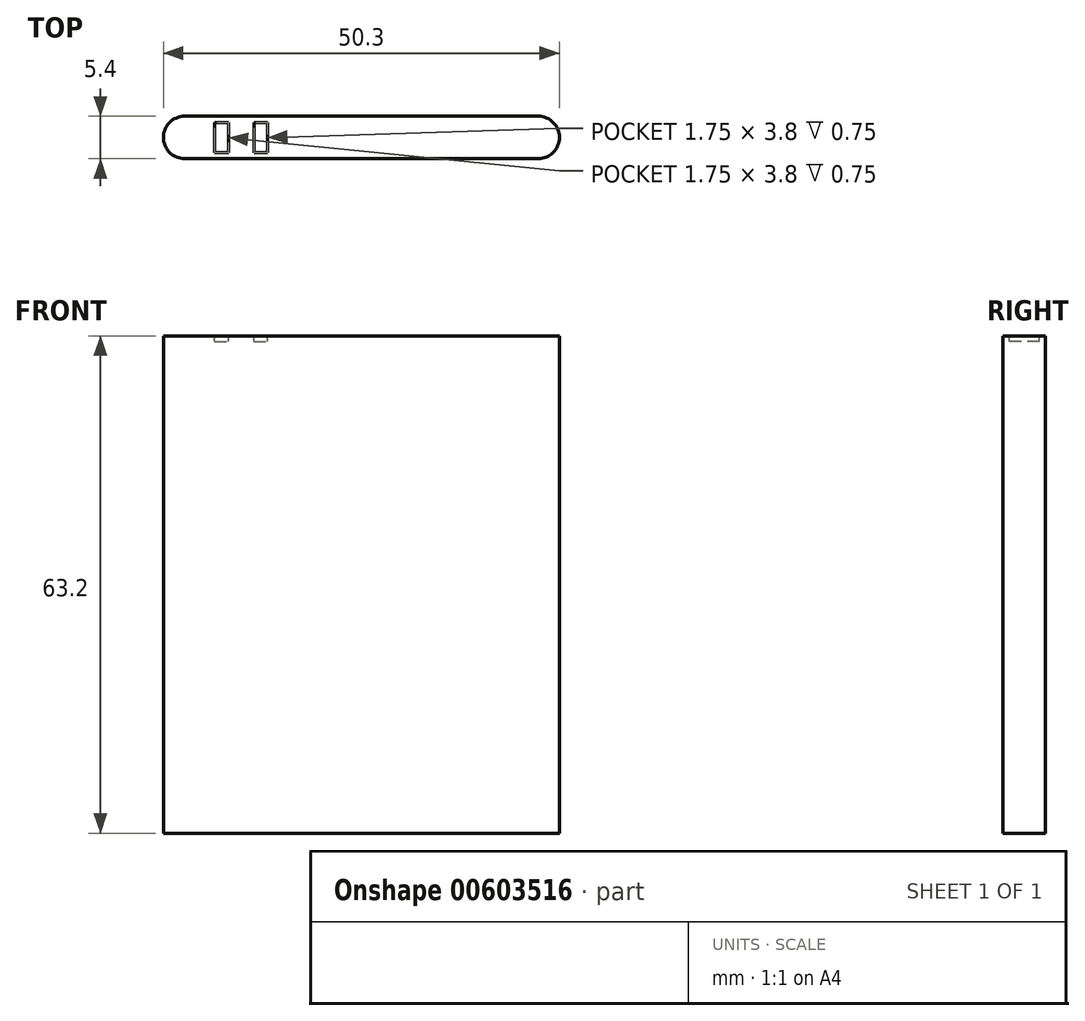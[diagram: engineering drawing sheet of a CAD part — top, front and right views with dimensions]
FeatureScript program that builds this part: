
annotation { "Feature Type Name" : "Feature", "Feature Type Description" : "" }
export const myFeature = defineFeature(function(context is Context, id is Id, definition is map)
    precondition{}
    {
        {
            var Q0;
            Q0=qCreatedBy(makeId("Front.planeOp"),FACE);
            var sketch = newSketch(context, id + "F0", { "sketchPlane" : qUnion([Q0])});
            skLineSegment(sketch, "E0.bottom", {"start": v(25.15, -31.6) * mm, "end": v(-25.15, -31.6) * mm});
            skLineSegment(sketch, "E0.top", {"start": v(25.15, 31.6) * mm, "end": v(-25.15, 31.6) * mm});
            skLineSegment(sketch, "E0.left", {"start": v(25.15, -31.6) * mm, "end": v(25.15, 31.6) * mm});
            skLineSegment(sketch, "E0.right", {"start": v(-25.15, -31.6) * mm, "end": v(-25.15, 31.6) * mm});
            skPoint(sketch, "E0.middle", {"position": v(0, 0) * mm});
            skSolve(sketch);
        }
        {
            var Q0;
            Q0=makeQuery(id+"F0.imprint","IMPRINT",FACE,{"disambiguationData":[TD([[makeQuery(id+"F0.imprint","IMPRINT",EDGE,{"derivedFrom":sQuery(id+"F0.wireOp",EDGE,"E0.bottom")}),-1.0]])]});
            extrude(context, id + "F1", {"entities" : qUnion([Q0]), "endBound" : BoundingType.SYMMETRIC, "depth" : 5.4 * mm, "offsetDistance" : 25 * mm});
        }
        {
            var Q0;
            Q0=makeQuery(id+"F1.opExtrude","CAP_EDGE",EDGE,{"disambiguationData":[OSD([sQuery(id+"F0.wireOp",EDGE,"E0.left")])],"isStart":true});
            var Q1;
            Q1=makeQuery(id+"F1.opExtrude","CAP_EDGE",EDGE,{"disambiguationData":[OSD([sQuery(id+"F0.wireOp",EDGE,"E0.left")])],"isStart":false});
            var Q2;
            Q2=makeQuery(id+"F1.opExtrude","CAP_EDGE",EDGE,{"disambiguationData":[OSD([sQuery(id+"F0.wireOp",EDGE,"E0.right")])],"isStart":false});
            var Q3;
            Q3=makeQuery(id+"F1.opExtrude","CAP_EDGE",EDGE,{"disambiguationData":[OSD([sQuery(id+"F0.wireOp",EDGE,"E0.right")])],"isStart":true});
            fillet(context, id + "F2", {"entities" : qUnion([Q0, Q1, Q2, Q3]), "radius" : 2.7 * mm, "tangentPropagation" : true, "allowEdgeOverflow" : false});
        }
        {
            var Q0;
            Q0=makeQuery(id+"F1.opExtrude","SWEPT_FACE",FACE,{"disambiguationData":[OSD([sQuery(id+"F0.wireOp",EDGE,"E0.top")])]});
            var sketch = newSketch(context, id + "F3", { "sketchPlane" : qUnion([Q0])});
            skLineSegment(sketch, "E1", {"start": v(-24.37, 1.9) * mm, "end": v(24.37, 1.9) * mm, "construction": true});
            skLineSegment(sketch, "E2", {"start": v(-24.37, -1.9) * mm, "end": v(24.37, -1.9) * mm, "construction": true});
            skLineSegment(sketch, "E3.0.0", {"start": v(22.45, 2.7) * mm, "end": v(-22.45, 2.7) * mm, "construction": true});
            skArc(sketch, "E3.0.1", {"start": v(-22.45, 2.7) * mm, "mid": v(-25.15, 0) * mm, "end": v(-22.45, -2.7) * mm, "construction": true});
            skLineSegment(sketch, "E3.0.2", {"start": v(-22.45, -2.7) * mm, "end": v(22.45, -2.7) * mm, "construction": true});
            skArc(sketch, "E3.0.3", {"start": v(22.45, -2.7) * mm, "mid": v(25.15, 0) * mm, "end": v(22.45, 2.7) * mm, "construction": true});
            skLineSegment(sketch, "E4.bottom", {"start": v(-18.65, 1.9) * mm, "end": v(-16.9, 1.9) * mm});
            skLineSegment(sketch, "E4.top", {"start": v(-18.65, -1.9) * mm, "end": v(-16.9, -1.9) * mm});
            skLineSegment(sketch, "E4.left", {"start": v(-18.65, 1.9) * mm, "end": v(-18.65, -1.9) * mm});
            skLineSegment(sketch, "E4.right", {"start": v(-16.9, 1.9) * mm, "end": v(-16.9, -1.9) * mm});
            skLineSegment(sketch, "E5.bottom", {"start": v(-13.65, 1.9) * mm, "end": v(-11.9, 1.9) * mm});
            skLineSegment(sketch, "E5.top", {"start": v(-13.65, -1.9) * mm, "end": v(-11.9, -1.9) * mm});
            skLineSegment(sketch, "E5.left", {"start": v(-13.65, 1.9) * mm, "end": v(-13.65, -1.9) * mm});
            skLineSegment(sketch, "E5.right", {"start": v(-11.9, 1.9) * mm, "end": v(-11.9, -1.9) * mm});
            skSolve(sketch);
        }
        {
            var Q0;
            Q0=makeQuery(id+"F3.imprint","IMPRINT",FACE,{"disambiguationData":[TD([[makeQuery(id+"F3.imprint","IMPRINT",EDGE,{"derivedFrom":sQuery(id+"F3.wireOp",EDGE,"E4.bottom")}),-1.0]])]});
            var Q1;
            Q1=makeQuery(id+"F3.imprint","IMPRINT",FACE,{"disambiguationData":[TD([[makeQuery(id+"F3.imprint","IMPRINT",EDGE,{"derivedFrom":sQuery(id+"F3.wireOp",EDGE,"E5.bottom")}),-1.0]])]});
            extrude(context, id + "F4", {"entities" : qUnion([Q0, Q1]), "operationType" : NewBodyOperationType.REMOVE, "oppositeDirection" : true, "depth" : 0.75 * mm, "offsetDistance" : 25 * mm});
        }
    });
